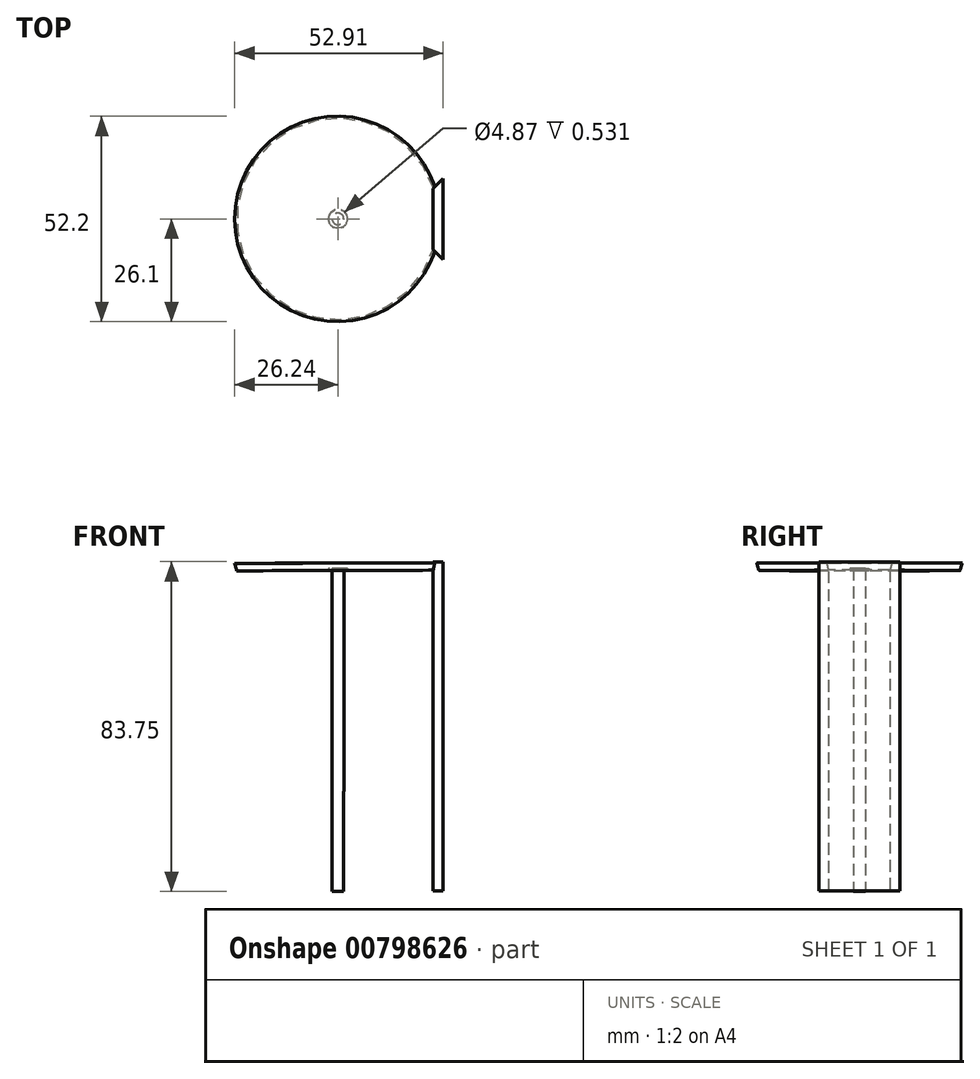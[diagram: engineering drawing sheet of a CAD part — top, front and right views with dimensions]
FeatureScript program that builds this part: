
annotation { "Feature Type Name" : "Feature", "Feature Type Description" : "" }
export const myFeature = defineFeature(function(context is Context, id is Id, definition is map)
    precondition{}
    {
        {
            var Q0;
            Q0=qCreatedBy(makeId("Front.planeOp"),FACE);
            var sketch = newSketch(context, id + "F0", { "sketchPlane" : qUnion([Q0])});
            skPoint(sketch, "E0", {"position": v(0.03, -0.02) * mm});
            skPoint(sketch, "E1", {"position": v(3.18, 1.13) * mm});
            skPoint(sketch, "E2", {"position": v(5.18, 2.5) * mm});
            skPoint(sketch, "E3", {"position": v(6.84, 4.37) * mm});
            skPoint(sketch, "E4", {"position": v(8.16, 5.94) * mm});
            skPoint(sketch, "E5", {"position": v(9.14, 7.52) * mm});
            skPoint(sketch, "E6", {"position": v(9.9, 8.84) * mm});
            skPoint(sketch, "E7", {"position": v(10.89, 10.54) * mm});
            skPoint(sketch, "E8", {"position": v(11.75, 12.1) * mm});
            skPoint(sketch, "E9", {"position": v(12.46, 13.83) * mm});
            skPoint(sketch, "E10", {"position": v(13.16, 15.1) * mm});
            skPoint(sketch, "E11", {"position": v(13.63, 16.27) * mm});
            skPoint(sketch, "E12", {"position": v(14.18, 17.52) * mm});
            skPoint(sketch, "E13", {"position": v(14.76, 19.04) * mm});
            skPoint(sketch, "E14", {"position": v(15.34, 20.55) * mm});
            skPoint(sketch, "E15", {"position": v(15.91, 22.07) * mm});
            skPoint(sketch, "E16", {"position": v(16.5, 23.66) * mm});
            skPoint(sketch, "E17", {"position": v(17, 25.39) * mm});
            skPoint(sketch, "E18", {"position": v(17.57, 26.83) * mm});
            skPoint(sketch, "E19", {"position": v(18.15, 28.78) * mm});
            skPoint(sketch, "E20", {"position": v(18.73, 30.87) * mm});
            skPoint(sketch, "E21", {"position": v(19.45, 32.97) * mm});
            skPoint(sketch, "E22", {"position": v(20.25, 35.58) * mm});
            skPoint(sketch, "E23", {"position": v(20.68, 37.74) * mm});
            skPoint(sketch, "E24", {"position": v(21.38, 39.85) * mm});
            skPoint(sketch, "E25", {"position": v(22, 42.1) * mm});
            skPoint(sketch, "E26", {"position": v(22.47, 44.2) * mm});
            skPoint(sketch, "E27", {"position": v(23.18, 47) * mm});
            skPoint(sketch, "E28", {"position": v(24.03, 50.12) * mm});
            skPoint(sketch, "E29", {"position": v(24.81, 53.4) * mm});
            skPoint(sketch, "E30", {"position": v(25.43, 56.2) * mm});
            skPoint(sketch, "E31", {"position": v(25.43, 58.07) * mm});
            skFitSpline(sketch, "E32", {"points": [v(0.03, -0.02) * mm, v(3.18, 1.13) * mm, v(5.18, 2.5) * mm, v(6.84, 4.37) * mm, v(8.16, 5.94) * mm, v(9.14, 7.52) * mm, v(9.9, 8.84) * mm, v(10.89, 10.54) * mm, v(11.75, 12.1) * mm, v(12.46, 13.83) * mm, v(13.16, 15.1) * mm, v(13.63, 16.27) * mm, v(14.18, 17.52) * mm, v(14.76, 19.04) * mm, v(15.34, 20.55) * mm, v(17.57, 26.83) * mm, v(19.45, 32.97) * mm, v(21.38, 39.85) * mm, v(24.81, 53.4) * mm, v(25.43, 56.2) * mm, v(25.95, 58.07) * mm], "startDerivative": vector(61.74, 19.66) * mm, "endDerivative": vector(13.33, 46) * mm});
            skLineSegment(sketch, "E33", {"start": v(25.95, 58.07) * mm, "end": v(-0.15, 58.07) * mm});
            skLineSegment(sketch, "E34", {"start": v(-0.15, 58.07) * mm, "end": v(0.03, -0.02) * mm});
            skLineSegment(sketch, "E35", {"start": v(19.45, 32.97) * mm, "end": v(-0.07, 32.97) * mm});
            skLineSegment(sketch, "E36", {"start": v(25.43, 56.2) * mm, "end": v(-0.14, 56.12) * mm});
            skLineSegment(sketch, "E37", {"start": v(23.97, 45.58) * mm, "end": v(-6.54, 45.48) * mm});
            skLineSegment(sketch, "E38", {"start": v(-4.68, 53.8) * mm, "end": v(34.04, 53.8) * mm});
            skLineSegment(sketch, "E39", {"start": v(-7.24, 50.6) * mm, "end": v(41.15, 50.6) * mm});
            skLineSegment(sketch, "E40", {"start": v(-7.24, 47.74) * mm, "end": v(38.8, 47.74) * mm});
            skLineSegment(sketch, "E41", {"start": v(-6.54, 43.31) * mm, "end": v(33.08, 43.31) * mm});
            skLineSegment(sketch, "E42", {"start": v(-6.61, 40.8) * mm, "end": v(35.36, 40.8) * mm});
            skLineSegment(sketch, "E43", {"start": v(-6.34, 38.08) * mm, "end": v(33.86, 38.08) * mm});
            skLineSegment(sketch, "E44", {"start": v(-4.24, 35.28) * mm, "end": v(35.36, 35.4) * mm});
            skLineSegment(sketch, "E45", {"start": v(-4.66, 30.97) * mm, "end": v(35.36, 30.97) * mm});
            skLineSegment(sketch, "E46", {"start": v(-4.61, 28.25) * mm, "end": v(32.86, 28.25) * mm});
            skLineSegment(sketch, "E47", {"start": v(-4.44, 25.54) * mm, "end": v(32.3, 25.54) * mm});
            skLineSegment(sketch, "E48", {"start": v(-4.61, 22.96) * mm, "end": v(29.5, 22.96) * mm});
            skLineSegment(sketch, "E49", {"start": v(-4.36, 20.74) * mm, "end": v(30.66, 20.74) * mm});
            skLineSegment(sketch, "E50", {"start": v(-4.32, 18.64) * mm, "end": v(26.14, 18.64) * mm});
            skLineSegment(sketch, "E51", {"start": v(-4.53, 16.42) * mm, "end": v(28.75, 16.42) * mm});
            skLineSegment(sketch, "E52", {"start": v(-4.37, 14.08) * mm, "end": v(25.46, 14.08) * mm});
            skLineSegment(sketch, "E53", {"start": v(-4.32, 11.86) * mm, "end": v(28.46, 11.86) * mm});
            skLineSegment(sketch, "E54", {"start": v(-4.25, 9.7) * mm, "end": v(25.28, 9.7) * mm});
            skLineSegment(sketch, "E55", {"start": v(-4.22, 7.66) * mm, "end": v(30.42, 7.66) * mm});
            skLineSegment(sketch, "E56", {"start": v(-4.18, 5.62) * mm, "end": v(24.54, 5.7) * mm});
            skLineSegment(sketch, "E57", {"start": v(-4.14, 3.23) * mm, "end": v(12.44, 3.23) * mm});
            skLineSegment(sketch, "E58", {"start": v(-4.34, 1.53) * mm, "end": v(8.85, 1.53) * mm});
            skSolve(sketch);
        }
        {
            var Q0;
            {var subQ0=sQuery(id+"F0.wireOp",EDGE,"E33");Q0=makeQuery(id+"F0.imprint","IMPRINT",FACE,{"disambiguationData":[TD([[makeQuery(id+"F0.imprint","IMPRINT",EDGE,{"derivedFrom":subQ0}),1.0]])]});}
            var Q1;
            Q1=sQuery(id+"F0.wireOp",EDGE,"E34");
            revolve(context, id + "F1", {"surfaceOperationType" : NewSurfaceOperationType.NEW, "entities" : qUnion([Q0]), "axis" : qUnion([Q1]), "revolveType" : RevolveType.FULL});
        }
        {
            var Q0;
            Q0=qCreatedBy(makeId("Top.planeOp"),FACE);
            var sketch = newSketch(context, id + "F2", { "sketchPlane" : qUnion([Q0])});
            skCircle(sketch, "E59", {"center": v(0, 0) * mm, "radius": 2.44 * mm});
            skSolve(sketch);
        }
        {
            var Q0;
            Q0=makeQuery(id+"F2.imprint","IMPRINT",FACE,{"disambiguationData":[TD([[makeQuery(id+"F2.imprint","IMPRINT",EDGE,{"derivedFrom":sQuery(id+"F2.wireOp",EDGE,"E59")}),1.0]])]});
            extrude(context, id + "F3", {"entities" : qUnion([Q0]), "operationType" : NewBodyOperationType.REMOVE, "depth" : 56.64 * mm, "offsetDistance" : 25.4 * mm});
        }
        {
            var Q0;
            Q0=qCreatedBy(makeId("Top.planeOp"),FACE);
            var sketch = newSketch(context, id + "F4", { "sketchPlane" : qUnion([Q0])});
            skCircle(sketch, "E60", {"center": v(0, 0) * mm, "radius": 1.48 * mm});
            skSolve(sketch);
        }
        {
            var Q0;
            Q0=makeQuery(id+"F4.imprint","IMPRINT",FACE,{"disambiguationData":[TD([[makeQuery(id+"F4.imprint","IMPRINT",EDGE,{"derivedFrom":sQuery(id+"F4.wireOp",EDGE,"E60")}),1.0]])]});
            var Q1;
            Q1=sQuery(id+"F4.wireOp",EDGE,"E60");
            extrude(context, id + "F5", {"entities" : qUnion([Q0]), "operationType" : NewBodyOperationType.ADD, "surfaceEntities" : qUnion([Q1]), "depth" : 57.66 * mm, "offsetDistance" : 25.4 * mm});
        }
        {
            var Q0;
            Q0=makeQuery(id+"F5.opExtrude","CAP_FACE",FACE,{"disambiguationData":[OSD([sQuery(id+"F4.wireOp",EDGE,"E60")])],"isStart":true});
            cPlane(context, id + "F6", {"entities" : qUnion([Q0]), "cplaneType" : CPlaneType.OFFSET, "offset" : 25.4 * mm, "width" : 152.4 * mm, "height" : 152.4 * mm});
        }
        {
            var Q0;
            Q0=qCreatedBy(id+"F6.planeOp",FACE);
            var sketch = newSketch(context, id + "F7", { "sketchPlane" : qUnion([Q0])});
            skCircle(sketch, "E61", {"center": v(0, 0) * mm, "radius": 1.48 * mm});
            skSolve(sketch);
        }
        {
            var Q0;
            Q0=qSketchRegion(id+"F7",true);
            extrude(context, id + "F8", {"entities" : qUnion([Q0]), "operationType" : NewBodyOperationType.ADD, "oppositeDirection" : true, "depth" : 33.02 * mm, "offsetDistance" : 25.4 * mm});
        }
        {
            var Q0;
            Q0=qCreatedBy(makeId("Right.planeOp"),FACE);
            cPlane(context, id + "F9", {"entities" : qUnion([Q0]), "cplaneType" : CPlaneType.OFFSET, "offset" : 24.13 * mm, "width" : 152.4 * mm, "height" : 152.4 * mm});
        }
        {
            var Q0;
            Q0=qCreatedBy(id+"F9.planeOp",FACE);
            var sketch = newSketch(context, id + "F10", { "sketchPlane" : qUnion([Q0])});
            skLineSegment(sketch, "E62", {"start": v(0, 58.35) * mm, "end": v(-26.14, 58.35) * mm});
            skLineSegment(sketch, "E63", {"start": v(-26.14, 58.35) * mm, "end": v(26.05, 58.35) * mm});
            skLineSegment(sketch, "E64", {"start": v(0, 58.35) * mm, "end": v(0, -25.28) * mm});
            skLineSegment(sketch, "E65", {"start": v(0, 58.35) * mm, "end": v(12.8, 58.35) * mm});
            skLineSegment(sketch, "E66", {"start": v(12.8, 58.35) * mm, "end": v(12.8, -25.28) * mm});
            skLineSegment(sketch, "E67", {"start": v(12.8, -25.28) * mm, "end": v(-12.85, -25.28) * mm});
            skLineSegment(sketch, "E68", {"start": v(-12.85, -25.28) * mm, "end": v(-12.85, 58.35) * mm});
            skSolve(sketch);
        }
        {
            var Q0;
            {var subQ2=sQuery(id+"F10.wireOp",EDGE,"E64");Q0=makeQuery(id+"F10.imprint","IMPRINT",FACE,{"disambiguationData":[TD([[makeQuery(id+"F10.imprint","IMPRINT",EDGE,{"derivedFrom":subQ2}),-1.0]])]});}
            var Q1;
            {var subQ2=sQuery(id+"F10.wireOp",EDGE,"E64");Q1=makeQuery(id+"F10.imprint","IMPRINT",FACE,{"disambiguationData":[TD([[makeQuery(id+"F10.imprint","IMPRINT",EDGE,{"derivedFrom":subQ2}),1.0]])]});}
            extrude(context, id + "F11", {"entities" : qUnion([Q0, Q1]), "operationType" : NewBodyOperationType.ADD, "depth" : 2.54 * mm, "offsetDistance" : 25.4 * mm});
        }
        {
            var Q0;
            Q0=makeQuery(id+"F11.opExtrude","CAP_EDGE",EDGE,{"disambiguationData":[OSD([sQuery(id+"F10.wireOp",EDGE,"E66")])],"isStart":true});
            var Q1;
            Q1=makeQuery(id+"F11.opExtrude","CAP_EDGE",EDGE,{"disambiguationData":[OSD([sQuery(id+"F10.wireOp",EDGE,"E68")])],"isStart":true});
            chamfer(context, id + "F12", {"entities" : qUnion([Q0, Q1]), "width" : 5.08 * mm, "tangentPropagation" : true});
        }
    });
